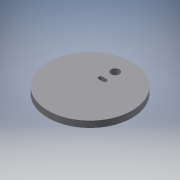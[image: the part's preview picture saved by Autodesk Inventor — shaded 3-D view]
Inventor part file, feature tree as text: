
AUTODESK INVENTOR PART (.ipt)
format: ipt  version: 2016 (Build 200138000, 138)  size: 107,008 bytes
history: native  units: mm
features: extrude x1, sketch x1
ambient origin geometry x8: Origin, YZ Plane, XZ Plane, XY Plane, X Axis, Y Axis, Z Axis, Center Point
bodies: Solid1 (feature_tree)
feature tree (2):
  extrude  "Extrusion1"  Depth=3.0mm
  sketch  "Sketch1"  dims[d0=40.0mm d1=4.0mm d2=4.0mm d3=2.0mm d4=1.0mm d5=12.0mm d6=5.0mm d7=3.0mm d8=0.0mm]
